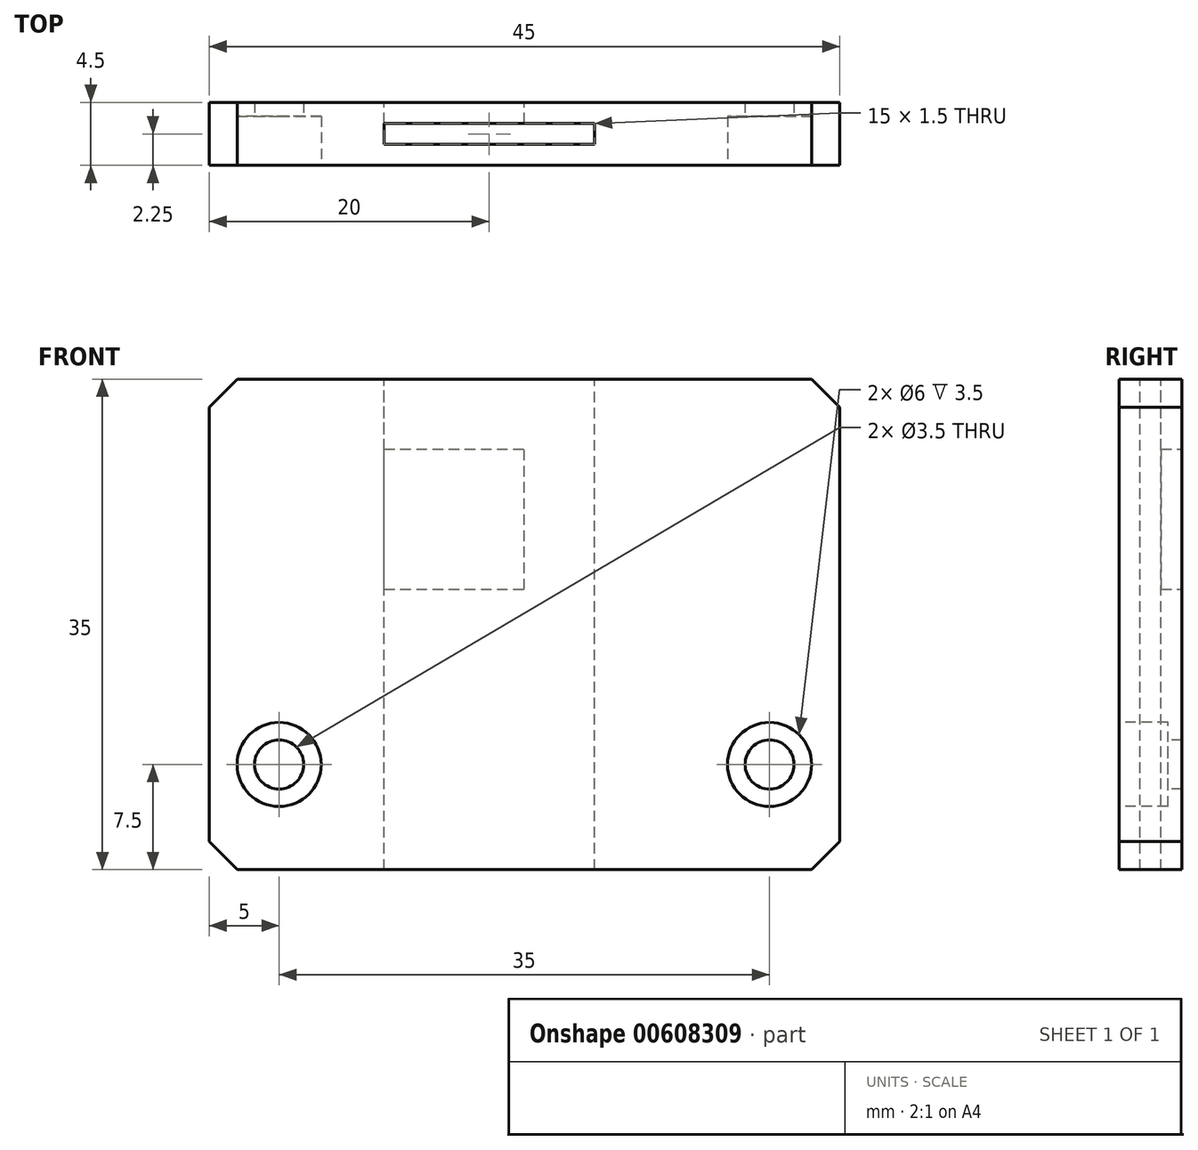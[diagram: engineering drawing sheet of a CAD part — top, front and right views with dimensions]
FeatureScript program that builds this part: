
annotation { "Feature Type Name" : "Feature", "Feature Type Description" : "" }
export const myFeature = defineFeature(function(context is Context, id is Id, definition is map)
    precondition{}
    {
        {
            var Q0;
            Q0=qCreatedBy(makeId("Front.planeOp"),FACE);
            var sketch = newSketch(context, id + "F0", { "sketchPlane" : qUnion([Q0])});
            skLineSegment(sketch, "E0.bottom", {"start": v(-22.5, 20) * mm, "end": v(22.5, 20) * mm});
            skLineSegment(sketch, "E0.top", {"start": v(-22.5, -15) * mm, "end": v(22.5, -15) * mm});
            skLineSegment(sketch, "E0.left", {"start": v(-22.5, 20) * mm, "end": v(-22.5, -15) * mm});
            skLineSegment(sketch, "E0.right", {"start": v(22.5, 20) * mm, "end": v(22.5, -15) * mm});
            skSolve(sketch);
        }
        {
            var Q0;
            Q0=makeQuery(id+"F0.imprint","IMPRINT",FACE,{"disambiguationData":[TD([[makeQuery(id+"F0.imprint","IMPRINT",EDGE,{"derivedFrom":sQuery(id+"F0.wireOp",EDGE,"E0.bottom")}),-1.0]])]});
            extrude(context, id + "F1", {"entities" : qUnion([Q0]), "depth" : 4.5 * mm, "offsetDistance" : 25 * mm});
        }
        {
            var Q0;
            Q0=makeQuery(id+"F1.opExtrude","SWEPT_FACE",FACE,{"disambiguationData":[OSD([sQuery(id+"F0.wireOp",EDGE,"E0.bottom")])]});
            var sketch = newSketch(context, id + "F2", { "sketchPlane" : qUnion([Q0])});
            skLineSegment(sketch, "E1.bottom", {"start": v(-10, -1.5) * mm, "end": v(5, -1.5) * mm});
            skLineSegment(sketch, "E1.top", {"start": v(-10, -3) * mm, "end": v(5, -3) * mm});
            skLineSegment(sketch, "E1.left", {"start": v(-10, -1.5) * mm, "end": v(-10, -3) * mm});
            skLineSegment(sketch, "E1.right", {"start": v(5, -1.5) * mm, "end": v(5, -3) * mm});
            skPoint(sketch, "E1.middle.positionSnap0", {"position": v(22.5, -2.25) * mm});
            skPoint(sketch, "E1.centerSnap0", {"position": v(22.5, -2.25) * mm});
            skSolve(sketch);
        }
        {
            var Q0;
            Q0 = qSketchRegion(id + "F2", true);
            extrude(context, id + "F3", {"entities" : qUnion([Q0]), "operationType" : NewBodyOperationType.REMOVE, "endBound" : BoundingType.THROUGH_ALL, "oppositeDirection" : true, "depth" : 25 * mm, "offsetDistance" : 25 * mm});
        }
        {
            var Q0;
            Q0=makeQuery(id+"F1.opExtrude","CAP_FACE",FACE,{"disambiguationData":[OSD([sQuery(id+"F0.wireOp",EDGE,"E0.bottom"),sQuery(id+"F0.wireOp",EDGE,"E0.top"),sQuery(id+"F0.wireOp",EDGE,"E0.left"),sQuery(id+"F0.wireOp",EDGE,"E0.right")])],"isStart":false});
            var sketch = newSketch(context, id + "F4", { "sketchPlane" : qUnion([Q0])});
            skCircle(sketch, "E2", {"center": v(17.5, -7.5) * mm, "radius": 3 * mm});
            skCircle(sketch, "E3.MirrorC", {"center": v(-17.5, -7.5) * mm, "radius": 3 * mm});
            skSolve(sketch);
        }
        {
            var Q0;
            Q0 = qSketchRegion(id + "F4", true);
            extrude(context, id + "F5", {"entities" : qUnion([Q0]), "operationType" : NewBodyOperationType.REMOVE, "oppositeDirection" : true, "depth" : 3.5 * mm, "offsetDistance" : 25 * mm});
        }
        {
            var Q0;
            Q0=makeQuery(id+"F1.opExtrude","CAP_FACE",FACE,{"disambiguationData":[OSD([sQuery(id+"F0.wireOp",EDGE,"E0.bottom"),sQuery(id+"F0.wireOp",EDGE,"E0.top"),sQuery(id+"F0.wireOp",EDGE,"E0.left"),sQuery(id+"F0.wireOp",EDGE,"E0.right")])],"isStart":false});
            var sketch = newSketch(context, id + "F6", { "sketchPlane" : qUnion([Q0])});
            skPoint(sketch, "E4", {"position": v(17.5, -7.5) * mm});
            skPoint(sketch, "E5", {"position": v(-17.5, -7.5) * mm});
            skCircle(sketch, "E6", {"center": v(17.5, -7.5) * mm, "radius": 1.75 * mm});
            skCircle(sketch, "E7", {"center": v(-17.5, -7.5) * mm, "radius": 1.75 * mm});
            skSolve(sketch);
        }
        {
            var Q0;
            Q0 = qSketchRegion(id + "F6", true);
            extrude(context, id + "F7", {"entities" : qUnion([Q0]), "operationType" : NewBodyOperationType.REMOVE, "endBound" : BoundingType.THROUGH_ALL, "oppositeDirection" : true, "depth" : 25 * mm, "offsetDistance" : 25 * mm});
        }
        {
            var Q0;
            Q0=makeQuery(id+"F1.opExtrude","CAP_FACE",FACE,{"disambiguationData":[OSD([sQuery(id+"F0.wireOp",EDGE,"E0.bottom"),sQuery(id+"F0.wireOp",EDGE,"E0.top"),sQuery(id+"F0.wireOp",EDGE,"E0.left"),sQuery(id+"F0.wireOp",EDGE,"E0.right")])],"isStart":true});
            var sketch = newSketch(context, id + "F8", { "sketchPlane" : qUnion([Q0])});
            skLineSegment(sketch, "E8.bottom", {"start": v(10, 5) * mm, "end": v(0, 5) * mm});
            skLineSegment(sketch, "E8.top", {"start": v(10, 15) * mm, "end": v(0, 15) * mm});
            skLineSegment(sketch, "E8.left", {"start": v(10, 5) * mm, "end": v(10, 15) * mm});
            skLineSegment(sketch, "E8.right", {"start": v(0, 5) * mm, "end": v(0, 15) * mm});
            skPoint(sketch, "E8.middle", {"position": v(0, 7) * mm});
            skSolve(sketch);
        }
        {
            var Q0;
            Q0 = qSketchRegion(id + "F8", true);
            extrude(context, id + "F9", {"entities" : qUnion([Q0]), "operationType" : NewBodyOperationType.REMOVE, "oppositeDirection" : true, "depth" : 3 * mm, "offsetDistance" : 25 * mm});
        }
        {
            var Q0;
            Q0=makeQuery(id+"F1.opExtrude","SWEPT_EDGE",EDGE,{"disambiguationData":[OSD([sQuery(id+"F0.wireOp",EDGE,"E0.bottom"),sQuery(id+"F0.wireOp",EDGE,"E0.left")])]});
            var Q1;
            Q1=makeQuery(id+"F1.opExtrude","SWEPT_EDGE",EDGE,{"disambiguationData":[OSD([sQuery(id+"F0.wireOp",EDGE,"E0.bottom"),sQuery(id+"F0.wireOp",EDGE,"E0.right")])]});
            var Q2;
            Q2=makeQuery(id+"F1.opExtrude","SWEPT_EDGE",EDGE,{"disambiguationData":[OSD([sQuery(id+"F0.wireOp",EDGE,"E0.top"),sQuery(id+"F0.wireOp",EDGE,"E0.right")])]});
            var Q3;
            Q3=makeQuery(id+"F1.opExtrude","SWEPT_EDGE",EDGE,{"disambiguationData":[OSD([sQuery(id+"F0.wireOp",EDGE,"E0.top"),sQuery(id+"F0.wireOp",EDGE,"E0.left")])]});
            chamfer(context, id + "F10", {"entities" : qUnion([Q0, Q1, Q2, Q3]), "width" : 2 * mm, "tangentPropagation" : true});
        }
    });
